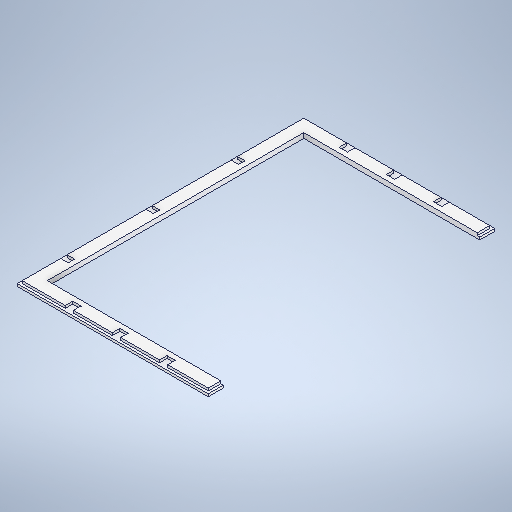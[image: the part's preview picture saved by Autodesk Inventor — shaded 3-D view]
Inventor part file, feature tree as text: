
AUTODESK INVENTOR PART (.ipt)
format: ipt  version: 2025 (Build 290162000, 162)  size: 890,880 bytes
history: native  units: in
note: dims shown in document units (in); Inventor stores cm internally (conversion verified against a paired STEP export)
features: projected_geometry x31, sketch x26, extrude x23, other x2, mirror x1
ambient origin geometry x8: Origin, YZ Plane, XZ Plane, XY Plane, X Axis, Y Axis, Z Axis, Center Point
bodies: Solid1 (feature_tree)
feature tree (83):
  extrude  "BasePlate"  Depth=9.0in
  other  "Template"
  extrude  "SunFounderBase"  Depth=0.2362in
  extrude  "SunfounderStuds"  Depth=0.0984in
  extrude  "RPiBase"  Depth=5.0787in
  extrude  "RPiStuds"  Depth=1.811in
  extrude  "VoltageConverter"  Depth=1.6325in
  extrude  "12VConverter"  Depth=0.0984in
  extrude  "12V2"  Depth=2.2835in
  extrude  "PoEBlock"  Depth=0.0787in
  extrude  "SunfounderSupport"  Depth=0.0787in
  extrude  "Latch12V"  Depth=0.1575in
  extrude  "L12V2"  Depth=0.0984in
  extrude  "LatchRpi"  Depth=0.1969in TaperAngle=0.0deg
  extrude  "LatchSunF"  Depth=0.0787in
  extrude  "LatchSunF2"  Depth=0.0787in
  extrude  "PoERemove"  Depth=0.1575in
  extrude  "EdgeCut"  Depth=0.0984in
  extrude  "LeftCuts"  Depth=0.1969in TaperAngle=0.0deg
  other  "LRMidplane"
  mirror  "RightCuts"
  extrude  "Extrusion24"  Depth=0.3937in
  extrude  "Extrusion25"  Depth=0.8in
  extrude  "Extrusion26"  Depth=0.3937in
  extrude  "Extrusion27"  Depth=0.1772in
  extrude  "Extrusion28"  Depth=0.1969in TaperAngle=0.0deg
  sketch  "Sketch1"  dims[d0=6.0in d1=9.0in]
  projected_geometry  "Projected Loop1"
  sketch  "Sketch3"  dims[d2=0.1575in d3=0.0in d4=0.2362in]
  sketch  "Sketch4"  dims[d6=0.2559in d7=0.0984in]
  projected_geometry  "Projected Loop2"
  projected_geometry  "Projected Loop3"
  projected_geometry  "Projected Loop4"
  projected_geometry  "Projected Loop5"
  sketch  "Sketch5"  dims[d8=1.8898in d9=5.0787in]
  sketch  "Sketch6"  dims[d14=0.1181in d15=1.811in]
  projected_geometry  "Projected Loop6"
  projected_geometry  "Projected Loop7"
  projected_geometry  "Projected Loop8"
  projected_geometry  "Projected Loop9"
  sketch  "Sketch7"  dims[d16=4.3012in d17=1.6325in]
  sketch  "Sketch8"  dims[d29=0.5118in d30=0.0984in]
  projected_geometry  "Projected Loop10"
  projected_geometry  "Projected Loop11"
  sketch  "Sketch9"  dims[d31=0.9055in d32=2.2835in]
  sketch  "Sketch10"  dims[d37=0.0787in d38=0.0787in]
  projected_geometry  "Projected Loop12"
  sketch  "Sketch11"  dims[d39=0.0787in d40=0.0787in]
  sketch  "Sketch14"  dims[d41=0.1575in d42=0.0in d43=0.0984in]
  projected_geometry  "Projected Loop16"
  projected_geometry  "Projected Loop17"
  sketch  "Sketch15"  dims[d44=0.0984in d45=0.0984in]
  projected_geometry  "Projected Loop18"
  sketch  "Sketch16"  dims[d46=0.0984in d47=0.1969in d48=0.0in]
  projected_geometry  "Projected Loop19"
  sketch  "Sketch17"  dims[d49=0.0787in d50=0.0787in]
  projected_geometry  "Projected Loop20"
  projected_geometry  "Projected Loop21"
  sketch  "Sketch18"  dims[d51=0.0787in d52=0.0787in]
  projected_geometry  "Projected Loop22"
  projected_geometry  "Projected Loop23"
  sketch  "Sketch19"  dims[d53=0.1575in d54=0.0in d55=0.0984in]
  projected_geometry  "Projected Loop24"
  projected_geometry  "Projected Loop25"
  sketch  "Sketch20"  dims[d56=0.0984in d57=0.0984in]
  sketch  "Sketch21"  dims[d58=0.0984in d59=0.1969in d60=0.0in]
  projected_geometry  "Projected Loop26"
  projected_geometry  "Projected Loop27"
  sketch  "Sketch22"  dims[d64=0.3937in d65=0.3937in]
  projected_geometry  "Projected Loop28"
  sketch  "Sketch23"  dims[d66=0.1772in d67=0.8in]
  projected_geometry  "Projected Loop29"
  sketch  "Sketch24"  dims[d68=0.3937in d69=0.3937in]
  projected_geometry  "Projected Loop30"
  sketch  "Sketch25"  dims[d70=0.1969in d71=0.0in d72=0.1772in]
  projected_geometry  "Projected Loop31"
  sketch  "Sketch26"  dims[d73=0.1772in d74=0.1969in d75=0.0in]
  projected_geometry  "Projected Loop32"
  sketch  "Sketch27"  dims[d76=0.063in]
  sketch  "Sketch28"  dims[d77=0.063in]
  projected_geometry  "Projected Loop33"
  sketch  "Sketch29"  dims[d78=0.1181in d79=0.0in d80=0.063in d81=0.1969in d82=0.1969in d83=0.1969in d84=0.1969in d85=0.1772in d86=0.0in d87=0.4724in d88=0.0in d96=0.1575in d97=0.0in d98=0.5118in d99=1.5748in d100=0.1969in d101=0.0in d102=0.1732in d103=0.0394in d104=0.2362in d105=0.1732in d106=0.1772in d107=0.0in d108=0.1772in d109=0.1772in d110=0.1969in d111=0.0in d114=2.3591in d115=1.9488in d116=0.0787in d117=0.0787in d118=0.0787in d119=0.3937in d120=0.3937in d121=0.1772in d122=0.1772in d123=0.1575in d124=0.0in d125=0.0394in d126=0.0in d127=1.1811in d128=2.3622in d129=0.2756in d130=0.2756in d131=0.1575in d132=0.0in d133=0.1772in d134=0.1772in d135=0.1969in d136=0.0in d137=0.315in d138=0.1969in d139=0.0in d140=0.0787in d141=0.0787in d142=0.0in d151=0.0787in d152=0.0in d155=1.288in d156=0.2in d157=2.475in d158=0.2in d159=2.475in d160=0.2in d161=0.315in d162=0.315in d163=0.315in d164=0.0787in d165=0.0in d173=0.26in d174=0.6299in d175=0.26in d176=0.6299in d177=0.26in d178=0.6299in d179=0.0787in d180=0.0787in d181=0.1575in d182=1.7687in d183=0.0in d184=1.7687in d185=0.0in d186=0.3937in d187=0.0in d188=0.3937in d189=0.0in]
  projected_geometry  "Projected Loop34"
